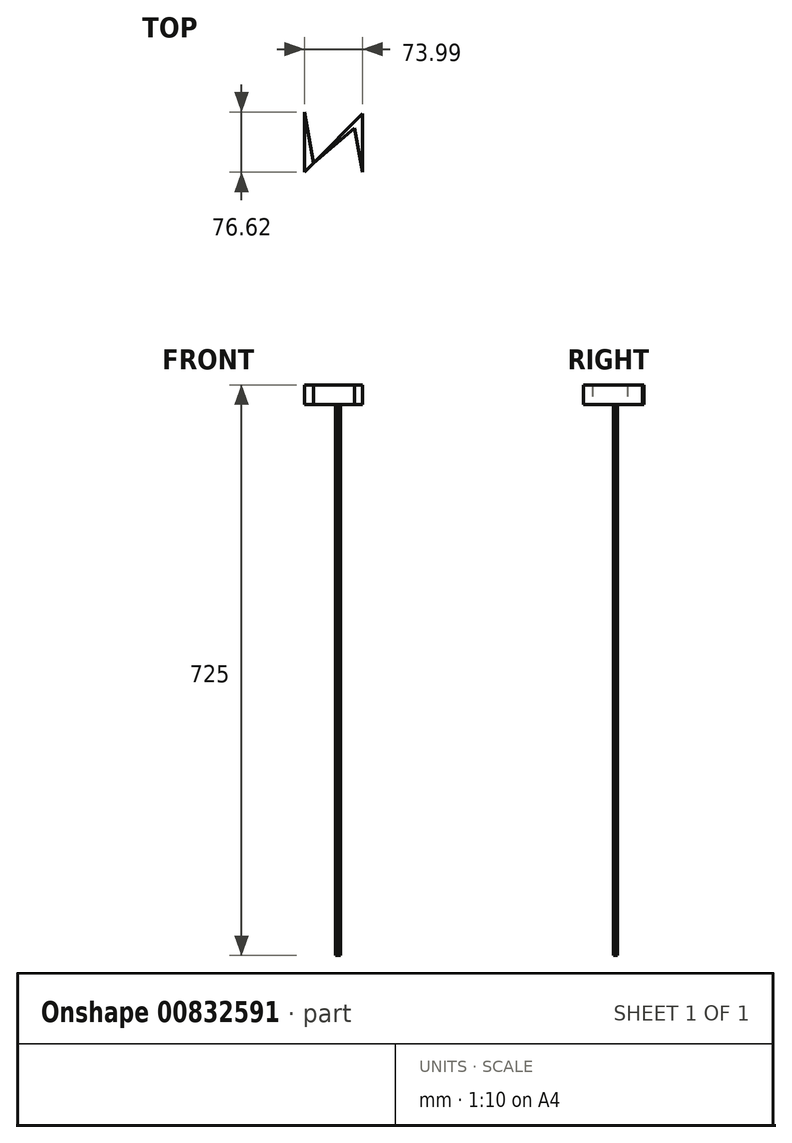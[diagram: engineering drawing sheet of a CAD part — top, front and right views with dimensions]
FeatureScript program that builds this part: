
annotation { "Feature Type Name" : "Feature", "Feature Type Description" : "" }
export const myFeature = defineFeature(function(context is Context, id is Id, definition is map)
    precondition{}
    {
        {
            var Q0;
            Q0=qCreatedBy(makeId("Top.planeOp"),FACE);
            var sketch = newSketch(context, id + "F0", { "sketchPlane" : qUnion([Q0])});
            skLineSegment(sketch, "E0", {"start": v(-54.55, 34.21) * mm, "end": v(-54.55, -42.4) * mm});
            skLineSegment(sketch, "E1", {"start": v(-54.55, -42.4) * mm, "end": v(19.44, 32.45) * mm});
            skLineSegment(sketch, "E2", {"start": v(19.44, 32.45) * mm, "end": v(19.44, -42.4) * mm});
            skLineSegment(sketch, "E3", {"start": v(-54.55, 34.21) * mm, "end": v(-43.02, -30.74) * mm});
            skLineSegment(sketch, "E4", {"start": v(-43.02, -30.74) * mm, "end": v(19.44, 22.47) * mm});
            skLineSegment(sketch, "E5", {"start": v(7.77, 20.65) * mm, "end": v(19.44, -42.4) * mm});
            skSolve(sketch);
        }
        {
            var Q0;
            {var subQ1=sQuery(id+"F0.wireOp",EDGE,"E1");var subQ3=sQuery(id+"F0.wireOp",EDGE,"E5");var subQ4=makeQuery(id+"F0.imprint","INTERSECT",VERTEX,{"derivedFrom":[subQ1,subQ3]});Q0=makeQuery(id+"F0.imprint","IMPRINT",FACE,{"disambiguationData":[TD([[makeQuery(id+"F0.imprint","IMPRINT",EDGE,{"disambiguationData":[TD([[subQ4,-1.0]])],"derivedFrom":subQ3}),-1.0]])]});}
            var Q1;
            {var subQ0=sQuery(id+"F0.wireOp",EDGE,"E5");var subQ1=sQuery(id+"F0.wireOp",EDGE,"E2");var subQ2=makeQuery(id+"F0.imprint","INTERSECT",VERTEX,{"derivedFrom":[subQ1,subQ0]});Q1=makeQuery(id+"F0.imprint","IMPRINT",FACE,{"disambiguationData":[TD([[makeQuery(id+"F0.imprint","IMPRINT",EDGE,{"disambiguationData":[TD([[subQ2,1.0]])],"derivedFrom":subQ1}),-1.0]])]});}
            var Q2;
            {var subQ0=sQuery(id+"F0.wireOp",EDGE,"E2");var subQ1=sQuery(id+"F0.wireOp",EDGE,"E1");var subQ2=makeQuery(id+"F0.imprint","INTERSECT",VERTEX,{"derivedFrom":[subQ1,subQ0]});Q2=makeQuery(id+"F0.imprint","IMPRINT",FACE,{"disambiguationData":[TD([[makeQuery(id+"F0.imprint","IMPRINT",EDGE,{"disambiguationData":[TD([[subQ2,1.0]])],"derivedFrom":subQ1}),-1.0]])]});}
            var Q3;
            {var subQ0=sQuery(id+"F0.wireOp",EDGE,"E0");Q3=makeQuery(id+"F0.imprint","IMPRINT",FACE,{"disambiguationData":[TD([[makeQuery(id+"F0.imprint","IMPRINT",EDGE,{"derivedFrom":subQ0}),1.0]])]});}
            extrude(context, id + "F1", {"entities" : qUnion([Q0, Q1, Q2, Q3]), "depth" : 25 * mm, "offsetDistance" : 25 * mm});
        }
        {
            var Q0;
            Q0=makeQuery(id+"F1.opExtrude","CAP_FACE",FACE,{"disambiguationData":[OSD([sQuery(id+"F0.wireOp",EDGE,"E1"),sQuery(id+"F0.wireOp",EDGE,"E2"),sQuery(id+"F0.wireOp",EDGE,"E4"),sQuery(id+"F0.wireOp",EDGE,"E5")])],"isStart":true});
            var sketch = newSketch(context, id + "F2", { "sketchPlane" : qUnion([Q0])});
            skCircle(sketch, "E6", {"center": v(-15.76, 7.52) * mm, "radius": 9.2 * mm});
            skCircle(sketch, "E7", {"center": v(-15.76, 7.52) * mm, "radius": 5.27 * mm});
            skSolve(sketch);
        }
        {
            var Q0;
            {var subQ0=sQuery(id+"F2.wireOp",EDGE,"E6");var subQ1=makeQuery(id+"F1.opExtrude","CAP_EDGE",EDGE,{"disambiguationData":[OSD([sQuery(id+"F0.wireOp",EDGE,"E4")])],"isStart":true});var subQ2=makeQuery(id+"F2.imprint","INTERSECT",VERTEX,{"disambiguationData":[OD(0.0)],"derivedFrom":[subQ1,subQ0]});Q0=makeQuery(id+"F2.imprint","IMPRINT",FACE,{"disambiguationData":[TD([[makeQuery(id+"F2.imprint","IMPRINT",EDGE,{"disambiguationData":[TD([[subQ2,1.0]])],"derivedFrom":subQ0}),1.0]])]});}
            var Q1;
            {var subQ0=sQuery(id+"F2.wireOp",EDGE,"E6");var subQ1=sQuery(id+"F0.wireOp",EDGE,"E1");var subQ2=makeQuery(id+"F0.imprint","INTERSECT",VERTEX,{"derivedFrom":[subQ1,sQuery(id+"F0.wireOp",EDGE,"E5")]});var subQ3=makeQuery(id+"F1.opExtrude","CAP_EDGE",EDGE,{"disambiguationData":[OSD([subQ1]),TDD([makeQuery(id+"F0.imprint","IMPRINT",EDGE,{"disambiguationData":[TD([[subQ2,1.0]])],"derivedFrom":subQ1}),makeQuery(id+"F0.imprint","IMPRINT",EDGE,{"disambiguationData":[TD([[makeQuery(id+"F0.imprint","INTERSECT",VERTEX,{"derivedFrom":[subQ1,sQuery(id+"F0.wireOp",EDGE,"E2")]}),1.0]])],"derivedFrom":subQ1})])],"isStart":true});var subQ4=makeQuery(id+"F2.imprint","INTERSECT",VERTEX,{"disambiguationData":[OD(0.0)],"derivedFrom":[subQ3,subQ0]});Q1=makeQuery(id+"F2.imprint","IMPRINT",FACE,{"disambiguationData":[TD([[makeQuery(id+"F2.imprint","IMPRINT",EDGE,{"disambiguationData":[TD([[subQ4,-1.0]])],"derivedFrom":subQ0}),1.0]])]});}
            extrude(context, id + "F3", {"entities" : qUnion([Q0, Q1]), "depth" : 700 * mm, "offsetDistance" : 25 * mm});
        }
    });
